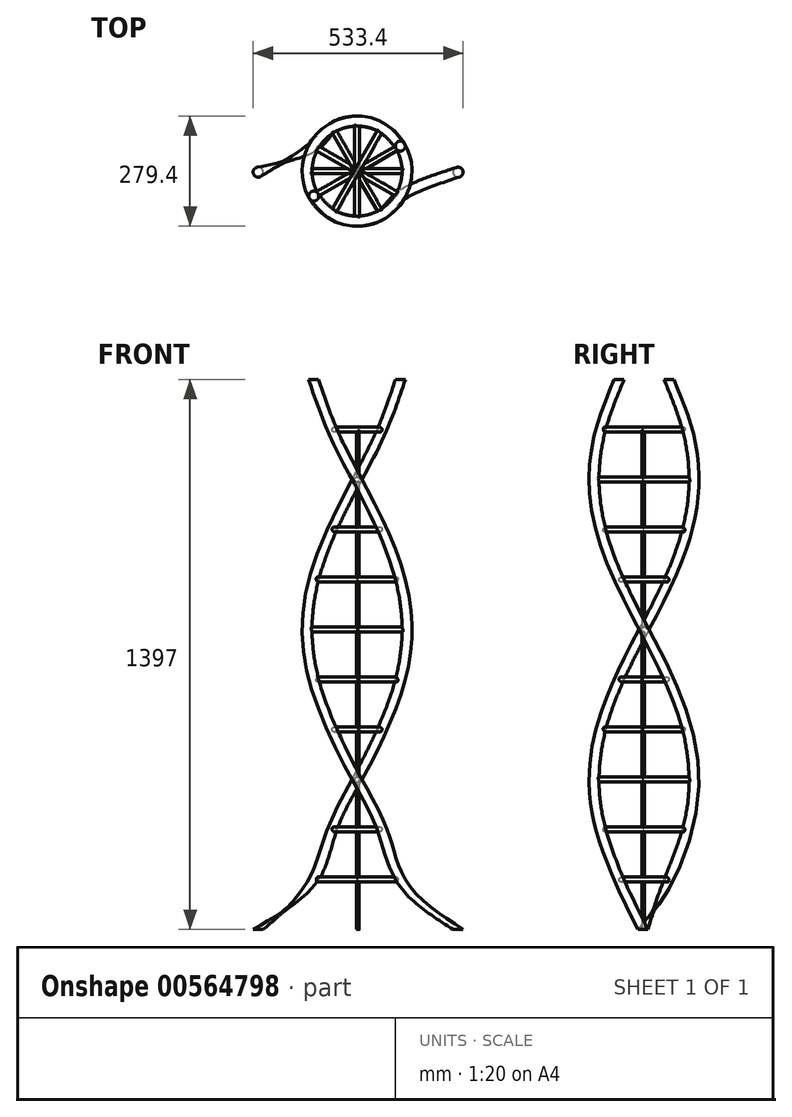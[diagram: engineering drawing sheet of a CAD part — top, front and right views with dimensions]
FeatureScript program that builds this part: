
annotation { "Feature Type Name" : "Feature", "Feature Type Description" : "" }
export const myFeature = defineFeature(function(context is Context, id is Id, definition is map)
    precondition{}
    {
        {
            var Q0;
            Q0=qCreatedBy(makeId("Top.planeOp"),FACE);
            var sketch = newSketch(context, id + "F0", { "sketchPlane" : qUnion([Q0])});
            skCircle(sketch, "E0", {"center": v(0, 0) * mm, "radius": 254 * mm, "construction": true});
            skLineSegment(sketch, "E1", {"start": v(219.97, -127) * mm, "end": v(-219.97, 127) * mm});
            skLineSegment(sketch, "E2", {"start": v(0, 0) * mm, "end": v(0, -254) * mm, "construction": true});
            skLineSegment(sketch, "E3", {"start": v(0, 0) * mm, "end": v(254, 0) * mm, "construction": true});
            skCircle(sketch, "E4", {"center": v(219.97, -127) * mm, "radius": 12.7 * mm});
            skLineSegment(sketch, "E5", {"start": v(127, -219.97) * mm, "end": v(-127, 219.97) * mm});
            skLineSegment(sketch, "E6", {"start": v(0, 254) * mm, "end": v(0, -254) * mm});
            skLineSegment(sketch, "E7.MirrorCS", {"start": v(-127, -219.97) * mm, "end": v(127, 219.97) * mm});
            skLineSegment(sketch, "E8.MirrorCS", {"start": v(-219.97, -127) * mm, "end": v(219.97, 127) * mm});
            skLineSegment(sketch, "E9", {"start": v(254, 0) * mm, "end": v(-254, 0) * mm});
            skCircle(sketch, "E10", {"center": v(127, -219.97) * mm, "radius": 12.7 * mm});
            skCircle(sketch, "E11", {"center": v(0, -254) * mm, "radius": 12.7 * mm});
            skCircle(sketch, "E12", {"center": v(-127, -219.97) * mm, "radius": 12.7 * mm});
            skCircle(sketch, "E13", {"center": v(-219.97, -127) * mm, "radius": 12.7 * mm});
            skCircle(sketch, "E14", {"center": v(-254, 0) * mm, "radius": 12.7 * mm});
            skCircle(sketch, "E15", {"center": v(-219.97, 127) * mm, "radius": 12.7 * mm});
            skCircle(sketch, "E16", {"center": v(-127, 219.97) * mm, "radius": 76.2 * mm});
            skCircle(sketch, "E17", {"center": v(0, 254) * mm, "radius": 76.2 * mm});
            skCircle(sketch, "E18", {"center": v(127, 219.97) * mm, "radius": 38.1 * mm});
            skCircle(sketch, "E19", {"center": v(219.97, 127) * mm, "radius": 38.1 * mm});
            skCircle(sketch, "E20", {"center": v(254, 0) * mm, "radius": 12.7 * mm});
            skSolve(sketch);
        }
        {
            var Q0;
            Q0=qCreatedBy(makeId("Top.planeOp"),FACE);
            cPlane(context, id + "F1", {"entities" : qUnion([Q0]), "cplaneType" : CPlaneType.OFFSET, "offset" : 127 * mm, "width" : 152.4 * mm, "height" : 152.4 * mm});
        }
        {
            var Q0;
            Q0=qCreatedBy(id+"F1.planeOp",FACE);
            cPlane(context, id + "F2", {"entities" : qUnion([Q0]), "cplaneType" : CPlaneType.OFFSET, "offset" : 127 * mm, "width" : 152.4 * mm, "height" : 152.4 * mm});
        }
        {
            var Q0;
            Q0=qCreatedBy(id+"F2.planeOp",FACE);
            cPlane(context, id + "F3", {"entities" : qUnion([Q0]), "cplaneType" : CPlaneType.OFFSET, "offset" : 127 * mm, "width" : 152.4 * mm, "height" : 152.4 * mm});
        }
        {
            var Q0;
            Q0=qCreatedBy(id+"F1.planeOp",FACE);
            var sketch = newSketch(context, id + "F4", { "sketchPlane" : qUnion([Q0])});
            skCircle(sketch, "E21", {"center": v(-2.76, 2.76) * mm, "radius": 127 * mm, "construction": true});
            skLineSegment(sketch, "E22", {"start": v(107.22, -60.74) * mm, "end": v(-112.75, 66.26) * mm});
            skLineSegment(sketch, "E23", {"start": v(-2.76, 2.76) * mm, "end": v(-2.76, -124.24) * mm, "construction": true});
            skLineSegment(sketch, "E24", {"start": v(-2.76, 2.76) * mm, "end": v(124.24, 2.76) * mm, "construction": true});
            skCircle(sketch, "E25", {"center": v(107.22, -60.74) * mm, "radius": 12.7 * mm});
            skLineSegment(sketch, "E26", {"start": v(60.74, -107.22) * mm, "end": v(-66.26, 112.75) * mm});
            skLineSegment(sketch, "E27", {"start": v(-2.76, 129.76) * mm, "end": v(-2.76, -124.24) * mm});
            skLineSegment(sketch, "E28.MirrorCS", {"start": v(-66.26, -107.22) * mm, "end": v(60.74, 112.75) * mm});
            skLineSegment(sketch, "E29.MirrorCS", {"start": v(-112.75, -60.74) * mm, "end": v(107.22, 66.26) * mm});
            skLineSegment(sketch, "E30", {"start": v(124.24, 2.76) * mm, "end": v(-129.76, 2.76) * mm});
            skCircle(sketch, "E31", {"center": v(60.74, -107.22) * mm, "radius": 12.7 * mm});
            skCircle(sketch, "E32", {"center": v(-2.76, -124.24) * mm, "radius": 12.7 * mm});
            skCircle(sketch, "E33", {"center": v(-66.26, -107.22) * mm, "radius": 12.7 * mm});
            skCircle(sketch, "E34", {"center": v(-112.75, -60.74) * mm, "radius": 12.7 * mm});
            skCircle(sketch, "E35", {"center": v(-129.76, 2.76) * mm, "radius": 12.7 * mm});
            skCircle(sketch, "E36", {"center": v(-112.75, 66.26) * mm, "radius": 12.7 * mm});
            skCircle(sketch, "E37", {"center": v(-66.26, 112.75) * mm, "radius": 12.7 * mm});
            skCircle(sketch, "E38", {"center": v(-2.76, 129.76) * mm, "radius": 12.7 * mm});
            skCircle(sketch, "E39", {"center": v(60.74, 112.75) * mm, "radius": 12.7 * mm});
            skCircle(sketch, "E40", {"center": v(107.22, 66.26) * mm, "radius": 12.7 * mm});
            skCircle(sketch, "E41", {"center": v(124.24, 2.76) * mm, "radius": 12.7 * mm});
            skSolve(sketch);
        }
        {
            var Q0;
            Q0=qCreatedBy(id+"F2.planeOp",FACE);
            var sketch = newSketch(context, id + "F5", { "sketchPlane" : qUnion([Q0])});
            skCircle(sketch, "E42", {"center": v(-2.76, 2.76) * mm, "radius": 127 * mm, "construction": true});
            skLineSegment(sketch, "E43", {"start": v(107.22, -60.74) * mm, "end": v(-112.75, 66.26) * mm});
            skLineSegment(sketch, "E44", {"start": v(-2.76, 2.76) * mm, "end": v(-2.76, -124.24) * mm, "construction": true});
            skLineSegment(sketch, "E45", {"start": v(-2.76, 2.76) * mm, "end": v(124.24, 2.76) * mm, "construction": true});
            skCircle(sketch, "E46", {"center": v(107.22, -60.74) * mm, "radius": 12.7 * mm});
            skLineSegment(sketch, "E47", {"start": v(60.74, -107.22) * mm, "end": v(-66.26, 112.75) * mm});
            skLineSegment(sketch, "E48", {"start": v(-2.76, 129.76) * mm, "end": v(-2.76, -124.24) * mm});
            skLineSegment(sketch, "E49.MirrorCS", {"start": v(-66.26, -107.22) * mm, "end": v(60.74, 112.75) * mm});
            skLineSegment(sketch, "E50.MirrorCS", {"start": v(-112.75, -60.74) * mm, "end": v(107.22, 66.26) * mm});
            skLineSegment(sketch, "E51", {"start": v(124.24, 2.76) * mm, "end": v(-129.76, 2.76) * mm});
            skCircle(sketch, "E52", {"center": v(60.74, -107.22) * mm, "radius": 12.7 * mm});
            skCircle(sketch, "E53", {"center": v(-2.76, -124.24) * mm, "radius": 12.7 * mm});
            skCircle(sketch, "E54", {"center": v(-66.26, -107.22) * mm, "radius": 12.7 * mm});
            skCircle(sketch, "E55", {"center": v(-112.75, -60.74) * mm, "radius": 12.7 * mm});
            skCircle(sketch, "E56", {"center": v(-129.76, 2.76) * mm, "radius": 12.7 * mm});
            skCircle(sketch, "E57", {"center": v(-112.75, 66.26) * mm, "radius": 12.7 * mm});
            skCircle(sketch, "E58", {"center": v(-66.26, 112.75) * mm, "radius": 12.7 * mm});
            skCircle(sketch, "E59", {"center": v(-2.76, 129.76) * mm, "radius": 12.7 * mm});
            skCircle(sketch, "E60", {"center": v(60.74, 112.75) * mm, "radius": 12.7 * mm});
            skCircle(sketch, "E61", {"center": v(107.22, 66.26) * mm, "radius": 12.7 * mm});
            skCircle(sketch, "E62", {"center": v(124.24, 2.76) * mm, "radius": 12.7 * mm});
            skSolve(sketch);
        }
        {
            var Q0;
            Q0=qCreatedBy(id+"F3.planeOp",FACE);
            var sketch = newSketch(context, id + "F6", { "sketchPlane" : qUnion([Q0])});
            skCircle(sketch, "E63", {"center": v(-2.76, 2.76) * mm, "radius": 127 * mm, "construction": true});
            skLineSegment(sketch, "E64", {"start": v(107.22, -60.74) * mm, "end": v(-112.75, 66.26) * mm});
            skLineSegment(sketch, "E65", {"start": v(-2.76, 2.76) * mm, "end": v(-2.76, -124.24) * mm, "construction": true});
            skLineSegment(sketch, "E66", {"start": v(-2.76, 2.76) * mm, "end": v(124.24, 2.76) * mm, "construction": true});
            skCircle(sketch, "E67", {"center": v(107.22, -60.74) * mm, "radius": 12.7 * mm});
            skLineSegment(sketch, "E68", {"start": v(60.74, -107.22) * mm, "end": v(-66.26, 112.75) * mm});
            skLineSegment(sketch, "E69", {"start": v(-2.76, 129.76) * mm, "end": v(-2.76, -124.24) * mm});
            skLineSegment(sketch, "E70.MirrorCS", {"start": v(-66.26, -107.22) * mm, "end": v(60.74, 112.75) * mm});
            skLineSegment(sketch, "E71.MirrorCS", {"start": v(-112.75, -60.74) * mm, "end": v(107.22, 66.26) * mm});
            skLineSegment(sketch, "E72", {"start": v(124.24, 2.76) * mm, "end": v(-129.76, 2.76) * mm});
            skCircle(sketch, "E73", {"center": v(60.74, -107.22) * mm, "radius": 12.7 * mm});
            skCircle(sketch, "E74", {"center": v(-2.76, -124.24) * mm, "radius": 12.7 * mm});
            skCircle(sketch, "E75", {"center": v(-66.26, -107.22) * mm, "radius": 12.7 * mm});
            skCircle(sketch, "E76", {"center": v(-112.75, -60.74) * mm, "radius": 12.7 * mm});
            skCircle(sketch, "E77", {"center": v(-129.76, 2.76) * mm, "radius": 12.7 * mm});
            skCircle(sketch, "E78", {"center": v(-112.75, 66.26) * mm, "radius": 12.7 * mm});
            skCircle(sketch, "E79", {"center": v(-66.26, 112.75) * mm, "radius": 12.7 * mm});
            skCircle(sketch, "E80", {"center": v(-2.76, 129.76) * mm, "radius": 12.7 * mm});
            skCircle(sketch, "E81", {"center": v(60.74, 112.75) * mm, "radius": 12.7 * mm});
            skCircle(sketch, "E82", {"center": v(107.22, 66.26) * mm, "radius": 12.7 * mm});
            skCircle(sketch, "E83", {"center": v(124.24, 2.76) * mm, "radius": 12.7 * mm});
            skSolve(sketch);
        }
        {
            var Q0;
            Q0=qCreatedBy(id+"F3.planeOp",FACE);
            cPlane(context, id + "F7", {"entities" : qUnion([Q0]), "cplaneType" : CPlaneType.OFFSET, "offset" : 127 * mm, "width" : 152.4 * mm, "height" : 152.4 * mm});
        }
        {
            var Q0;
            Q0=qCreatedBy(id+"F7.planeOp",FACE);
            cPlane(context, id + "F8", {"entities" : qUnion([Q0]), "cplaneType" : CPlaneType.OFFSET, "offset" : 127 * mm, "width" : 152.4 * mm, "height" : 152.4 * mm});
        }
        {
            var Q0;
            Q0=qCreatedBy(id+"F8.planeOp",FACE);
            cPlane(context, id + "F9", {"entities" : qUnion([Q0]), "cplaneType" : CPlaneType.OFFSET, "offset" : 127 * mm, "width" : 152.4 * mm, "height" : 152.4 * mm});
        }
        {
            var Q0;
            Q0=qCreatedBy(id+"F9.planeOp",FACE);
            cPlane(context, id + "F10", {"entities" : qUnion([Q0]), "cplaneType" : CPlaneType.OFFSET, "offset" : 127 * mm, "width" : 152.4 * mm, "height" : 152.4 * mm});
        }
        {
            var Q0;
            Q0=qCreatedBy(id+"F10.planeOp",FACE);
            cPlane(context, id + "F11", {"entities" : qUnion([Q0]), "cplaneType" : CPlaneType.OFFSET, "offset" : 127 * mm, "width" : 152.4 * mm, "height" : 152.4 * mm});
        }
        {
            var Q0;
            Q0=qCreatedBy(id+"F11.planeOp",FACE);
            cPlane(context, id + "F12", {"entities" : qUnion([Q0]), "cplaneType" : CPlaneType.OFFSET, "offset" : 127 * mm, "width" : 152.4 * mm, "height" : 152.4 * mm});
        }
        {
            var Q0;
            Q0=qCreatedBy(id+"F12.planeOp",FACE);
            cPlane(context, id + "F13", {"entities" : qUnion([Q0]), "cplaneType" : CPlaneType.OFFSET, "offset" : 127 * mm, "width" : 152.4 * mm, "height" : 152.4 * mm});
        }
        {
            var Q0;
            Q0=qCreatedBy(id+"F13.planeOp",FACE);
            cPlane(context, id + "F14", {"entities" : qUnion([Q0]), "cplaneType" : CPlaneType.OFFSET, "offset" : 127 * mm, "width" : 152.4 * mm, "height" : 152.4 * mm});
        }
        {
            var Q0;
            Q0=qCreatedBy(id+"F7.planeOp",FACE);
            var sketch = newSketch(context, id + "F15", { "sketchPlane" : qUnion([Q0])});
            skCircle(sketch, "E84", {"center": v(-2.76, 2.76) * mm, "radius": 127 * mm, "construction": true});
            skLineSegment(sketch, "E85", {"start": v(107.22, -60.74) * mm, "end": v(-112.75, 66.26) * mm});
            skLineSegment(sketch, "E86", {"start": v(-2.76, 2.76) * mm, "end": v(-2.76, -124.24) * mm, "construction": true});
            skLineSegment(sketch, "E87", {"start": v(-2.76, 2.76) * mm, "end": v(124.24, 2.76) * mm, "construction": true});
            skCircle(sketch, "E88", {"center": v(107.22, -60.74) * mm, "radius": 12.7 * mm});
            skLineSegment(sketch, "E89", {"start": v(60.74, -107.22) * mm, "end": v(-66.26, 112.75) * mm});
            skLineSegment(sketch, "E90", {"start": v(-2.76, 129.76) * mm, "end": v(-2.76, -124.24) * mm});
            skLineSegment(sketch, "E91.MirrorCS", {"start": v(-66.26, -107.22) * mm, "end": v(60.74, 112.75) * mm});
            skLineSegment(sketch, "E92.MirrorCS", {"start": v(-112.75, -60.74) * mm, "end": v(107.22, 66.26) * mm});
            skLineSegment(sketch, "E93", {"start": v(124.24, 2.76) * mm, "end": v(-129.76, 2.76) * mm});
            skCircle(sketch, "E94", {"center": v(60.74, -107.22) * mm, "radius": 12.7 * mm});
            skCircle(sketch, "E95", {"center": v(-2.76, -124.24) * mm, "radius": 12.7 * mm});
            skCircle(sketch, "E96", {"center": v(-66.26, -107.22) * mm, "radius": 12.7 * mm});
            skCircle(sketch, "E97", {"center": v(-112.75, -60.74) * mm, "radius": 12.7 * mm});
            skCircle(sketch, "E98", {"center": v(-129.76, 2.76) * mm, "radius": 12.7 * mm});
            skCircle(sketch, "E99", {"center": v(-112.75, 66.26) * mm, "radius": 12.7 * mm});
            skCircle(sketch, "E100", {"center": v(-66.26, 112.75) * mm, "radius": 12.7 * mm});
            skCircle(sketch, "E101", {"center": v(-2.76, 129.76) * mm, "radius": 12.7 * mm});
            skCircle(sketch, "E102", {"center": v(60.74, 112.75) * mm, "radius": 12.7 * mm});
            skCircle(sketch, "E103", {"center": v(107.22, 66.26) * mm, "radius": 12.7 * mm});
            skCircle(sketch, "E104", {"center": v(124.24, 2.76) * mm, "radius": 12.7 * mm});
            skSolve(sketch);
        }
        {
            var Q0;
            Q0=qCreatedBy(id+"F8.planeOp",FACE);
            var sketch = newSketch(context, id + "F16", { "sketchPlane" : qUnion([Q0])});
            skCircle(sketch, "E105", {"center": v(-2.76, 2.76) * mm, "radius": 127 * mm, "construction": true});
            skLineSegment(sketch, "E106", {"start": v(107.22, -60.74) * mm, "end": v(-112.75, 66.26) * mm});
            skLineSegment(sketch, "E107", {"start": v(-2.76, 2.76) * mm, "end": v(-2.76, -124.24) * mm, "construction": true});
            skLineSegment(sketch, "E108", {"start": v(-2.76, 2.76) * mm, "end": v(124.24, 2.76) * mm, "construction": true});
            skCircle(sketch, "E109", {"center": v(107.22, -60.74) * mm, "radius": 12.7 * mm});
            skLineSegment(sketch, "E110", {"start": v(60.74, -107.22) * mm, "end": v(-66.26, 112.75) * mm});
            skLineSegment(sketch, "E111", {"start": v(-2.76, 129.76) * mm, "end": v(-2.76, -124.24) * mm});
            skLineSegment(sketch, "E112.MirrorCS", {"start": v(-66.26, -107.22) * mm, "end": v(60.74, 112.75) * mm});
            skLineSegment(sketch, "E113.MirrorCS", {"start": v(-112.75, -60.74) * mm, "end": v(107.22, 66.26) * mm});
            skLineSegment(sketch, "E114", {"start": v(124.24, 2.76) * mm, "end": v(-129.76, 2.76) * mm});
            skCircle(sketch, "E115", {"center": v(60.74, -107.22) * mm, "radius": 12.7 * mm});
            skCircle(sketch, "E116", {"center": v(-2.76, -124.24) * mm, "radius": 12.7 * mm});
            skCircle(sketch, "E117", {"center": v(-66.26, -107.22) * mm, "radius": 12.7 * mm});
            skCircle(sketch, "E118", {"center": v(-112.75, -60.74) * mm, "radius": 12.7 * mm});
            skCircle(sketch, "E119", {"center": v(-129.76, 2.76) * mm, "radius": 12.7 * mm});
            skCircle(sketch, "E120", {"center": v(-112.75, 66.26) * mm, "radius": 12.7 * mm});
            skCircle(sketch, "E121", {"center": v(-66.26, 112.75) * mm, "radius": 12.7 * mm});
            skCircle(sketch, "E122", {"center": v(-2.76, 129.76) * mm, "radius": 12.7 * mm});
            skCircle(sketch, "E123", {"center": v(60.74, 112.75) * mm, "radius": 12.7 * mm});
            skCircle(sketch, "E124", {"center": v(107.22, 66.26) * mm, "radius": 12.7 * mm});
            skCircle(sketch, "E125", {"center": v(124.24, 2.76) * mm, "radius": 12.7 * mm});
            skSolve(sketch);
        }
        {
            var Q0;
            Q0=qCreatedBy(id+"F9.planeOp",FACE);
            var sketch = newSketch(context, id + "F17", { "sketchPlane" : qUnion([Q0])});
            skCircle(sketch, "E126", {"center": v(-2.76, 2.76) * mm, "radius": 127 * mm, "construction": true});
            skLineSegment(sketch, "E127", {"start": v(107.22, -60.74) * mm, "end": v(-112.75, 66.26) * mm});
            skLineSegment(sketch, "E128", {"start": v(-2.76, 2.76) * mm, "end": v(-2.76, -124.24) * mm, "construction": true});
            skLineSegment(sketch, "E129", {"start": v(-2.76, 2.76) * mm, "end": v(124.24, 2.76) * mm, "construction": true});
            skCircle(sketch, "E130", {"center": v(107.22, -60.74) * mm, "radius": 12.7 * mm});
            skLineSegment(sketch, "E131", {"start": v(60.74, -107.22) * mm, "end": v(-66.26, 112.75) * mm});
            skLineSegment(sketch, "E132", {"start": v(-2.76, 129.76) * mm, "end": v(-2.76, -124.24) * mm});
            skLineSegment(sketch, "E133.MirrorCS", {"start": v(-66.26, -107.22) * mm, "end": v(60.74, 112.75) * mm});
            skLineSegment(sketch, "E134.MirrorCS", {"start": v(-112.75, -60.74) * mm, "end": v(107.22, 66.26) * mm});
            skLineSegment(sketch, "E135", {"start": v(124.24, 2.76) * mm, "end": v(-129.76, 2.76) * mm});
            skCircle(sketch, "E136", {"center": v(60.74, -107.22) * mm, "radius": 12.7 * mm});
            skCircle(sketch, "E137", {"center": v(-2.76, -124.24) * mm, "radius": 12.7 * mm});
            skCircle(sketch, "E138", {"center": v(-66.26, -107.22) * mm, "radius": 12.7 * mm});
            skCircle(sketch, "E139", {"center": v(-112.75, -60.74) * mm, "radius": 12.7 * mm});
            skCircle(sketch, "E140", {"center": v(-129.76, 2.76) * mm, "radius": 12.7 * mm});
            skCircle(sketch, "E141", {"center": v(-112.75, 66.26) * mm, "radius": 12.7 * mm});
            skCircle(sketch, "E142", {"center": v(-66.26, 112.75) * mm, "radius": 12.7 * mm});
            skCircle(sketch, "E143", {"center": v(-2.76, 129.76) * mm, "radius": 12.7 * mm});
            skCircle(sketch, "E144", {"center": v(60.74, 112.75) * mm, "radius": 12.7 * mm});
            skCircle(sketch, "E145", {"center": v(107.22, 66.26) * mm, "radius": 12.7 * mm});
            skCircle(sketch, "E146", {"center": v(124.24, 2.76) * mm, "radius": 12.7 * mm});
            skSolve(sketch);
        }
        {
            var Q0;
            Q0=qCreatedBy(id+"F10.planeOp",FACE);
            var sketch = newSketch(context, id + "F18", { "sketchPlane" : qUnion([Q0])});
            skCircle(sketch, "E147", {"center": v(-2.76, 2.76) * mm, "radius": 127 * mm, "construction": true});
            skLineSegment(sketch, "E148", {"start": v(107.22, -60.74) * mm, "end": v(-112.75, 66.26) * mm});
            skLineSegment(sketch, "E149", {"start": v(-2.76, 2.76) * mm, "end": v(-2.76, -124.24) * mm, "construction": true});
            skLineSegment(sketch, "E150", {"start": v(-2.76, 2.76) * mm, "end": v(124.24, 2.76) * mm, "construction": true});
            skCircle(sketch, "E151", {"center": v(107.22, -60.74) * mm, "radius": 12.7 * mm});
            skLineSegment(sketch, "E152", {"start": v(60.74, -107.22) * mm, "end": v(-66.26, 112.75) * mm});
            skLineSegment(sketch, "E153", {"start": v(-2.76, 129.76) * mm, "end": v(-2.76, -124.24) * mm});
            skLineSegment(sketch, "E154.MirrorCS", {"start": v(-66.26, -107.22) * mm, "end": v(60.74, 112.75) * mm});
            skLineSegment(sketch, "E155.MirrorCS", {"start": v(-112.75, -60.74) * mm, "end": v(107.22, 66.26) * mm});
            skLineSegment(sketch, "E156", {"start": v(124.24, 2.76) * mm, "end": v(-129.76, 2.76) * mm});
            skCircle(sketch, "E157", {"center": v(60.74, -107.22) * mm, "radius": 12.7 * mm});
            skCircle(sketch, "E158", {"center": v(-2.76, -124.24) * mm, "radius": 12.7 * mm});
            skCircle(sketch, "E159", {"center": v(-66.26, -107.22) * mm, "radius": 12.7 * mm});
            skCircle(sketch, "E160", {"center": v(-112.75, -60.74) * mm, "radius": 12.7 * mm});
            skCircle(sketch, "E161", {"center": v(-129.76, 2.76) * mm, "radius": 12.7 * mm});
            skCircle(sketch, "E162", {"center": v(-112.75, 66.26) * mm, "radius": 12.7 * mm});
            skCircle(sketch, "E163", {"center": v(-66.26, 112.75) * mm, "radius": 12.7 * mm});
            skCircle(sketch, "E164", {"center": v(-2.76, 129.76) * mm, "radius": 12.7 * mm});
            skCircle(sketch, "E165", {"center": v(60.74, 112.75) * mm, "radius": 12.7 * mm});
            skCircle(sketch, "E166", {"center": v(107.22, 66.26) * mm, "radius": 12.7 * mm});
            skCircle(sketch, "E167", {"center": v(124.24, 2.76) * mm, "radius": 12.7 * mm});
            skSolve(sketch);
        }
        {
            var Q0;
            Q0=qCreatedBy(id+"F11.planeOp",FACE);
            var sketch = newSketch(context, id + "F19", { "sketchPlane" : qUnion([Q0])});
            skCircle(sketch, "E168", {"center": v(-2.76, 2.76) * mm, "radius": 127 * mm, "construction": true});
            skLineSegment(sketch, "E169", {"start": v(107.22, -60.74) * mm, "end": v(-112.75, 66.26) * mm});
            skLineSegment(sketch, "E170", {"start": v(-2.76, 2.76) * mm, "end": v(-2.76, -124.24) * mm, "construction": true});
            skLineSegment(sketch, "E171", {"start": v(-2.76, 2.76) * mm, "end": v(124.24, 2.76) * mm, "construction": true});
            skCircle(sketch, "E172", {"center": v(107.22, -60.74) * mm, "radius": 12.7 * mm});
            skLineSegment(sketch, "E173", {"start": v(60.74, -107.22) * mm, "end": v(-66.26, 112.75) * mm});
            skLineSegment(sketch, "E174", {"start": v(-2.76, 129.76) * mm, "end": v(-2.76, -124.24) * mm});
            skLineSegment(sketch, "E175.MirrorCS", {"start": v(-66.26, -107.22) * mm, "end": v(60.74, 112.75) * mm});
            skLineSegment(sketch, "E176.MirrorCS", {"start": v(-112.75, -60.74) * mm, "end": v(107.22, 66.26) * mm});
            skLineSegment(sketch, "E177", {"start": v(124.24, 2.76) * mm, "end": v(-129.76, 2.76) * mm});
            skCircle(sketch, "E178", {"center": v(60.74, -107.22) * mm, "radius": 12.7 * mm});
            skCircle(sketch, "E179", {"center": v(-2.76, -124.24) * mm, "radius": 12.7 * mm});
            skCircle(sketch, "E180", {"center": v(-66.26, -107.22) * mm, "radius": 12.7 * mm});
            skCircle(sketch, "E181", {"center": v(-112.75, -60.74) * mm, "radius": 12.7 * mm});
            skCircle(sketch, "E182", {"center": v(-129.76, 2.76) * mm, "radius": 12.7 * mm});
            skCircle(sketch, "E183", {"center": v(-112.75, 66.26) * mm, "radius": 12.7 * mm});
            skCircle(sketch, "E184", {"center": v(-66.26, 112.75) * mm, "radius": 12.7 * mm});
            skCircle(sketch, "E185", {"center": v(-2.76, 129.76) * mm, "radius": 12.7 * mm});
            skCircle(sketch, "E186", {"center": v(60.74, 112.75) * mm, "radius": 12.7 * mm});
            skCircle(sketch, "E187", {"center": v(107.22, 66.26) * mm, "radius": 12.7 * mm});
            skCircle(sketch, "E188", {"center": v(124.24, 2.76) * mm, "radius": 12.7 * mm});
            skSolve(sketch);
        }
        {
            var Q0;
            Q0=qCreatedBy(id+"F12.planeOp",FACE);
            var sketch = newSketch(context, id + "F20", { "sketchPlane" : qUnion([Q0])});
            skCircle(sketch, "E189", {"center": v(-2.76, 2.76) * mm, "radius": 127 * mm, "construction": true});
            skLineSegment(sketch, "E190", {"start": v(107.22, -60.74) * mm, "end": v(-112.75, 66.26) * mm});
            skLineSegment(sketch, "E191", {"start": v(-2.76, 2.76) * mm, "end": v(-2.76, -124.24) * mm, "construction": true});
            skLineSegment(sketch, "E192", {"start": v(-2.76, 2.76) * mm, "end": v(124.24, 2.76) * mm, "construction": true});
            skCircle(sketch, "E193", {"center": v(107.22, -60.74) * mm, "radius": 12.7 * mm});
            skLineSegment(sketch, "E194", {"start": v(60.74, -107.22) * mm, "end": v(-66.26, 112.75) * mm});
            skLineSegment(sketch, "E195", {"start": v(-2.76, 129.76) * mm, "end": v(-2.76, -124.24) * mm});
            skLineSegment(sketch, "E196.MirrorCS", {"start": v(-66.26, -107.22) * mm, "end": v(60.74, 112.75) * mm});
            skLineSegment(sketch, "E197.MirrorCS", {"start": v(-112.75, -60.74) * mm, "end": v(107.22, 66.26) * mm});
            skLineSegment(sketch, "E198", {"start": v(124.24, 2.76) * mm, "end": v(-129.76, 2.76) * mm});
            skCircle(sketch, "E199", {"center": v(60.74, -107.22) * mm, "radius": 12.7 * mm});
            skCircle(sketch, "E200", {"center": v(-2.76, -124.24) * mm, "radius": 12.7 * mm});
            skCircle(sketch, "E201", {"center": v(-66.26, -107.22) * mm, "radius": 12.7 * mm});
            skCircle(sketch, "E202", {"center": v(-112.75, -60.74) * mm, "radius": 12.7 * mm});
            skCircle(sketch, "E203", {"center": v(-129.76, 2.76) * mm, "radius": 12.7 * mm});
            skCircle(sketch, "E204", {"center": v(-112.75, 66.26) * mm, "radius": 12.7 * mm});
            skCircle(sketch, "E205", {"center": v(-66.26, 112.75) * mm, "radius": 12.7 * mm});
            skCircle(sketch, "E206", {"center": v(-2.76, 129.76) * mm, "radius": 12.7 * mm});
            skCircle(sketch, "E207", {"center": v(60.74, 112.75) * mm, "radius": 12.7 * mm});
            skCircle(sketch, "E208", {"center": v(107.22, 66.26) * mm, "radius": 12.7 * mm});
            skCircle(sketch, "E209", {"center": v(124.24, 2.76) * mm, "radius": 12.7 * mm});
            skSolve(sketch);
        }
        {
            var Q0;
            Q0=qCreatedBy(id+"F13.planeOp",FACE);
            var sketch = newSketch(context, id + "F21", { "sketchPlane" : qUnion([Q0])});
            skCircle(sketch, "E210", {"center": v(-2.76, 2.76) * mm, "radius": 127 * mm, "construction": true});
            skLineSegment(sketch, "E211", {"start": v(107.22, -60.74) * mm, "end": v(-112.75, 66.26) * mm});
            skLineSegment(sketch, "E212", {"start": v(-2.76, 2.76) * mm, "end": v(-2.76, -124.24) * mm, "construction": true});
            skLineSegment(sketch, "E213", {"start": v(-2.76, 2.76) * mm, "end": v(124.24, 2.76) * mm, "construction": true});
            skCircle(sketch, "E214", {"center": v(107.22, -60.74) * mm, "radius": 12.7 * mm});
            skLineSegment(sketch, "E215", {"start": v(60.74, -107.22) * mm, "end": v(-66.26, 112.75) * mm});
            skLineSegment(sketch, "E216", {"start": v(-2.76, 129.76) * mm, "end": v(-2.76, -124.24) * mm});
            skLineSegment(sketch, "E217.MirrorCS", {"start": v(-66.26, -107.22) * mm, "end": v(60.74, 112.75) * mm});
            skLineSegment(sketch, "E218.MirrorCS", {"start": v(-112.75, -60.74) * mm, "end": v(107.22, 66.26) * mm});
            skLineSegment(sketch, "E219", {"start": v(124.24, 2.76) * mm, "end": v(-129.76, 2.76) * mm});
            skCircle(sketch, "E220", {"center": v(60.74, -107.22) * mm, "radius": 12.7 * mm});
            skCircle(sketch, "E221", {"center": v(-2.76, -124.24) * mm, "radius": 12.7 * mm});
            skCircle(sketch, "E222", {"center": v(-66.26, -107.22) * mm, "radius": 12.7 * mm});
            skCircle(sketch, "E223", {"center": v(-112.75, -60.74) * mm, "radius": 12.7 * mm});
            skCircle(sketch, "E224", {"center": v(-129.76, 2.76) * mm, "radius": 12.7 * mm});
            skCircle(sketch, "E225", {"center": v(-112.75, 66.26) * mm, "radius": 12.7 * mm});
            skCircle(sketch, "E226", {"center": v(-66.26, 112.75) * mm, "radius": 12.7 * mm});
            skCircle(sketch, "E227", {"center": v(-2.76, 129.76) * mm, "radius": 12.7 * mm});
            skCircle(sketch, "E228", {"center": v(60.74, 112.75) * mm, "radius": 12.7 * mm});
            skCircle(sketch, "E229", {"center": v(107.22, 66.26) * mm, "radius": 12.7 * mm});
            skCircle(sketch, "E230", {"center": v(124.24, 2.76) * mm, "radius": 12.7 * mm});
            skSolve(sketch);
        }
        {
            var Q0;
            Q0=qCreatedBy(id+"F14.planeOp",FACE);
            var sketch = newSketch(context, id + "F22", { "sketchPlane" : qUnion([Q0])});
            skCircle(sketch, "E231", {"center": v(-2.76, 2.76) * mm, "radius": 127 * mm, "construction": true});
            skLineSegment(sketch, "E232", {"start": v(107.22, -60.74) * mm, "end": v(-112.75, 66.26) * mm});
            skLineSegment(sketch, "E233", {"start": v(-2.76, 2.76) * mm, "end": v(-2.76, -124.24) * mm, "construction": true});
            skLineSegment(sketch, "E234", {"start": v(-2.76, 2.76) * mm, "end": v(124.24, 2.76) * mm, "construction": true});
            skCircle(sketch, "E235", {"center": v(107.22, -60.74) * mm, "radius": 12.7 * mm});
            skLineSegment(sketch, "E236", {"start": v(60.74, -107.22) * mm, "end": v(-66.26, 112.75) * mm});
            skLineSegment(sketch, "E237", {"start": v(-2.76, 129.76) * mm, "end": v(-2.76, -124.24) * mm});
            skLineSegment(sketch, "E238.MirrorCS", {"start": v(-66.26, -107.22) * mm, "end": v(60.74, 112.75) * mm});
            skLineSegment(sketch, "E239.MirrorCS", {"start": v(-112.75, -60.74) * mm, "end": v(107.22, 66.26) * mm});
            skLineSegment(sketch, "E240", {"start": v(124.24, 2.76) * mm, "end": v(-129.76, 2.76) * mm});
            skCircle(sketch, "E241", {"center": v(60.74, -107.22) * mm, "radius": 12.7 * mm});
            skCircle(sketch, "E242", {"center": v(-2.76, -124.24) * mm, "radius": 12.7 * mm});
            skCircle(sketch, "E243", {"center": v(-66.26, -107.22) * mm, "radius": 12.7 * mm});
            skCircle(sketch, "E244", {"center": v(-112.75, -60.74) * mm, "radius": 12.7 * mm});
            skCircle(sketch, "E245", {"center": v(-129.76, 2.76) * mm, "radius": 12.7 * mm});
            skCircle(sketch, "E246", {"center": v(-112.75, 66.26) * mm, "radius": 12.7 * mm});
            skCircle(sketch, "E247", {"center": v(-66.26, 112.75) * mm, "radius": 12.7 * mm});
            skCircle(sketch, "E248", {"center": v(-2.76, 129.76) * mm, "radius": 12.7 * mm});
            skCircle(sketch, "E249", {"center": v(60.74, 112.75) * mm, "radius": 12.7 * mm});
            skCircle(sketch, "E250", {"center": v(107.22, 66.26) * mm, "radius": 12.7 * mm});
            skCircle(sketch, "E251", {"center": v(124.24, 2.76) * mm, "radius": 12.7 * mm});
            skSolve(sketch);
        }
        {
            var Q0;
            Q0=makeQuery(id+"F0.imprint","IMPRINT",FACE,{"disambiguationData":[TD([[makeQuery(id+"F0.imprint","IMPRINT",EDGE,{"derivedFrom":sQuery(id+"F0.wireOp",EDGE,"E14")}),1.0]])]});
            var Q1;
            Q1=makeQuery(id+"F4.imprint","IMPRINT",FACE,{"disambiguationData":[TD([[makeQuery(id+"F4.imprint","IMPRINT",EDGE,{"derivedFrom":sQuery(id+"F4.wireOp",EDGE,"E36")}),1.0]])]});
            var Q2;
            Q2=makeQuery(id+"F5.imprint","IMPRINT",FACE,{"disambiguationData":[TD([[makeQuery(id+"F5.imprint","IMPRINT",EDGE,{"derivedFrom":sQuery(id+"F5.wireOp",EDGE,"E58")}),1.0]])]});
            var Q3;
            Q3=makeQuery(id+"F6.imprint","IMPRINT",FACE,{"disambiguationData":[TD([[makeQuery(id+"F6.imprint","IMPRINT",EDGE,{"derivedFrom":sQuery(id+"F6.wireOp",EDGE,"E80")}),1.0]])]});
            var Q4;
            Q4=makeQuery(id+"F15.imprint","IMPRINT",FACE,{"disambiguationData":[TD([[makeQuery(id+"F15.imprint","IMPRINT",EDGE,{"derivedFrom":sQuery(id+"F15.wireOp",EDGE,"E102")}),1.0]])]});
            var Q5;
            Q5=makeQuery(id+"F16.imprint","IMPRINT",FACE,{"disambiguationData":[TD([[makeQuery(id+"F16.imprint","IMPRINT",EDGE,{"derivedFrom":sQuery(id+"F16.wireOp",EDGE,"E124")}),1.0]])]});
            var Q6;
            Q6=makeQuery(id+"F17.imprint","IMPRINT",FACE,{"disambiguationData":[TD([[makeQuery(id+"F17.imprint","IMPRINT",EDGE,{"derivedFrom":sQuery(id+"F17.wireOp",EDGE,"E146")}),1.0]])]});
            var Q7;
            Q7=makeQuery(id+"F18.imprint","IMPRINT",FACE,{"disambiguationData":[TD([[makeQuery(id+"F18.imprint","IMPRINT",EDGE,{"derivedFrom":sQuery(id+"F18.wireOp",EDGE,"E151")}),1.0]])]});
            var Q8;
            Q8=makeQuery(id+"F19.imprint","IMPRINT",FACE,{"disambiguationData":[TD([[makeQuery(id+"F19.imprint","IMPRINT",EDGE,{"derivedFrom":sQuery(id+"F19.wireOp",EDGE,"E178")}),1.0]])]});
            var Q9;
            Q9=makeQuery(id+"F20.imprint","IMPRINT",FACE,{"disambiguationData":[TD([[makeQuery(id+"F20.imprint","IMPRINT",EDGE,{"derivedFrom":sQuery(id+"F20.wireOp",EDGE,"E200")}),1.0]])]});
            var Q10;
            Q10=makeQuery(id+"F21.imprint","IMPRINT",FACE,{"disambiguationData":[TD([[makeQuery(id+"F21.imprint","IMPRINT",EDGE,{"derivedFrom":sQuery(id+"F21.wireOp",EDGE,"E222")}),1.0]])]});
            var Q11;
            Q11=makeQuery(id+"F22.imprint","IMPRINT",FACE,{"disambiguationData":[TD([[makeQuery(id+"F22.imprint","IMPRINT",EDGE,{"derivedFrom":sQuery(id+"F22.wireOp",EDGE,"E244")}),1.0]])]});
            loft(context, id + "F23", {"sheetProfilesArray" : [{ "sheetProfileEntities" : qUnion([Q0]) }, { "sheetProfileEntities" : qUnion([Q1]) }, { "sheetProfileEntities" : qUnion([Q2]) }, { "sheetProfileEntities" : qUnion([Q3]) }, { "sheetProfileEntities" : qUnion([Q4]) }, { "sheetProfileEntities" : qUnion([Q5]) }, { "sheetProfileEntities" : qUnion([Q6]) }, { "sheetProfileEntities" : qUnion([Q7]) }, { "sheetProfileEntities" : qUnion([Q8]) }, { "sheetProfileEntities" : qUnion([Q9]) }, { "sheetProfileEntities" : qUnion([Q10]) }, { "sheetProfileEntities" : qUnion([Q11]) }]});
        }
        {
            var Q0;
            Q0=makeQuery(id+"F0.imprint","IMPRINT",FACE,{"disambiguationData":[TD([[makeQuery(id+"F0.imprint","IMPRINT",EDGE,{"derivedFrom":sQuery(id+"F0.wireOp",EDGE,"E20")}),1.0]])]});
            var Q1;
            Q1=makeQuery(id+"F4.imprint","IMPRINT",FACE,{"disambiguationData":[TD([[makeQuery(id+"F4.imprint","IMPRINT",EDGE,{"derivedFrom":sQuery(id+"F4.wireOp",EDGE,"E25")}),1.0]])]});
            var Q2;
            Q2=makeQuery(id+"F5.imprint","IMPRINT",FACE,{"disambiguationData":[TD([[makeQuery(id+"F5.imprint","IMPRINT",EDGE,{"derivedFrom":sQuery(id+"F5.wireOp",EDGE,"E52")}),1.0]])]});
            var Q3;
            Q3=makeQuery(id+"F6.imprint","IMPRINT",FACE,{"disambiguationData":[TD([[makeQuery(id+"F6.imprint","IMPRINT",EDGE,{"derivedFrom":sQuery(id+"F6.wireOp",EDGE,"E74")}),1.0]])]});
            var Q4;
            Q4=makeQuery(id+"F15.imprint","IMPRINT",FACE,{"disambiguationData":[TD([[makeQuery(id+"F15.imprint","IMPRINT",EDGE,{"derivedFrom":sQuery(id+"F15.wireOp",EDGE,"E96")}),1.0]])]});
            var Q5;
            Q5=makeQuery(id+"F16.imprint","IMPRINT",FACE,{"disambiguationData":[TD([[makeQuery(id+"F16.imprint","IMPRINT",EDGE,{"derivedFrom":sQuery(id+"F16.wireOp",EDGE,"E118")}),1.0]])]});
            var Q6;
            Q6=makeQuery(id+"F17.imprint","IMPRINT",FACE,{"disambiguationData":[TD([[makeQuery(id+"F17.imprint","IMPRINT",EDGE,{"derivedFrom":sQuery(id+"F17.wireOp",EDGE,"E140")}),1.0]])]});
            var Q7;
            Q7=makeQuery(id+"F18.imprint","IMPRINT",FACE,{"disambiguationData":[TD([[makeQuery(id+"F18.imprint","IMPRINT",EDGE,{"derivedFrom":sQuery(id+"F18.wireOp",EDGE,"E162")}),1.0]])]});
            var Q8;
            Q8=makeQuery(id+"F19.imprint","IMPRINT",FACE,{"disambiguationData":[TD([[makeQuery(id+"F19.imprint","IMPRINT",EDGE,{"derivedFrom":sQuery(id+"F19.wireOp",EDGE,"E184")}),1.0]])]});
            var Q9;
            Q9=makeQuery(id+"F20.imprint","IMPRINT",FACE,{"disambiguationData":[TD([[makeQuery(id+"F20.imprint","IMPRINT",EDGE,{"derivedFrom":sQuery(id+"F20.wireOp",EDGE,"E206")}),1.0]])]});
            var Q10;
            Q10=makeQuery(id+"F21.imprint","IMPRINT",FACE,{"disambiguationData":[TD([[makeQuery(id+"F21.imprint","IMPRINT",EDGE,{"derivedFrom":sQuery(id+"F21.wireOp",EDGE,"E228")}),1.0]])]});
            var Q11;
            Q11=makeQuery(id+"F22.imprint","IMPRINT",FACE,{"disambiguationData":[TD([[makeQuery(id+"F22.imprint","IMPRINT",EDGE,{"derivedFrom":sQuery(id+"F22.wireOp",EDGE,"E250")}),1.0]])]});
            loft(context, id + "F24", {"sheetProfilesArray" : [{ "sheetProfileEntities" : qUnion([Q0]) }, { "sheetProfileEntities" : qUnion([Q1]) }, { "sheetProfileEntities" : qUnion([Q2]) }, { "sheetProfileEntities" : qUnion([Q3]) }, { "sheetProfileEntities" : qUnion([Q4]) }, { "sheetProfileEntities" : qUnion([Q5]) }, { "sheetProfileEntities" : qUnion([Q6]) }, { "sheetProfileEntities" : qUnion([Q7]) }, { "sheetProfileEntities" : qUnion([Q8]) }, { "sheetProfileEntities" : qUnion([Q9]) }, { "sheetProfileEntities" : qUnion([Q10]) }, { "sheetProfileEntities" : qUnion([Q11]) }]});
        }
        {
            var Q0;
            Q0=sQuery(id+"F4.wireOp",VERTEX,"E25.center");
            var Q1;
            Q1=sQuery(id+"F4.wireOp",EDGE,"E22");
            cPlane(context, id + "F25", {"entities" : qUnion([Q0, Q1]), "cplaneType" : CPlaneType.LINE_POINT, "offset" : 25.4 * mm, "width" : 152.4 * mm, "height" : 152.4 * mm});
        }
        {
            var Q0;
            Q0=qCreatedBy(id+"F25.planeOp",FACE);
            var sketch = newSketch(context, id + "F26", { "sketchPlane" : qUnion([Q0])});
            skCircle(sketch, "E252", {"center": v(-1.01, 127) * mm, "radius": 6.35 * mm});
            skSolve(sketch);
        }
        {
            var Q0;
            Q0=makeQuery(id+"F26.imprint","IMPRINT",FACE,{"disambiguationData":[TD([[makeQuery(id+"F26.imprint","IMPRINT",EDGE,{"derivedFrom":sQuery(id+"F26.wireOp",EDGE,"E252")}),1.0]])]});
            var Q1;
            Q1=sQuery(id+"F4.wireOp",EDGE,"E22");
            sweep(context, id + "F27", {"operationType" : NewBodyOperationType.ADD, "profiles" : qUnion([Q0]), "path" : qUnion([Q1])});
        }
        {
            var Q0;
            Q0=sQuery(id+"F5.wireOp",VERTEX,"E47.start");
            var Q1;
            Q1=sQuery(id+"F5.wireOp",EDGE,"E47");
            cPlane(context, id + "F28", {"entities" : qUnion([Q0, Q1]), "cplaneType" : CPlaneType.LINE_POINT, "offset" : 25.4 * mm, "width" : 152.4 * mm, "height" : 152.4 * mm});
        }
        {
            var Q0;
            Q0=qCreatedBy(id+"F28.planeOp",FACE);
            var sketch = newSketch(context, id + "F29", { "sketchPlane" : qUnion([Q0])});
            skCircle(sketch, "E253", {"center": v(1.01, 254) * mm, "radius": 6.35 * mm});
            skSolve(sketch);
        }
        {
            var Q0;
            Q0 = qSketchRegion(id + "F29", true);
            var Q1;
            Q1=sQuery(id+"F29.wireOp",EDGE,"E253");
            var Q2;
            Q2=sQuery(id+"F5.wireOp",EDGE,"E47");
            sweep(context, id + "F30", {"operationType" : NewBodyOperationType.ADD, "profiles" : qUnion([Q0]), "surfaceProfiles" : qUnion([Q1]), "path" : qUnion([Q2])});
        }
        {
            var Q0;
            Q0=sQuery(id+"F6.wireOp",VERTEX,"E69.end");
            var Q1;
            Q1=sQuery(id+"F6.wireOp",EDGE,"E69");
            cPlane(context, id + "F31", {"entities" : qUnion([Q0, Q1]), "cplaneType" : CPlaneType.LINE_POINT, "offset" : 25.4 * mm, "width" : 152.4 * mm, "height" : 152.4 * mm});
        }
        {
            var Q0;
            Q0=qCreatedBy(id+"F31.planeOp",FACE);
            var sketch = newSketch(context, id + "F32", { "sketchPlane" : qUnion([Q0])});
            skCircle(sketch, "E254", {"center": v(-2.76, 381) * mm, "radius": 6.35 * mm});
            skSolve(sketch);
        }
        {
            var Q0;
            Q0 = qSketchRegion(id + "F32", true);
            var Q1;
            Q1=sQuery(id+"F6.wireOp",EDGE,"E69");
            sweep(context, id + "F33", {"operationType" : NewBodyOperationType.ADD, "profiles" : qUnion([Q0]), "path" : qUnion([Q1])});
        }
        {
            var Q0;
            Q0=sQuery(id+"F15.wireOp",VERTEX,"E96.center");
            var Q1;
            Q1=sQuery(id+"F15.wireOp",EDGE,"E91.MirrorCS");
            cPlane(context, id + "F34", {"entities" : qUnion([Q0, Q1]), "cplaneType" : CPlaneType.LINE_POINT, "offset" : 25.4 * mm, "width" : 152.4 * mm, "height" : 152.4 * mm});
        }
        {
            var Q0;
            Q0=qCreatedBy(id+"F34.planeOp",FACE);
            var sketch = newSketch(context, id + "F35", { "sketchPlane" : qUnion([Q0])});
            skCircle(sketch, "E255", {"center": v(3.77, 508) * mm, "radius": 6.35 * mm});
            skSolve(sketch);
        }
        {
            var Q0;
            Q0 = qSketchRegion(id + "F35", true);
            var Q1;
            Q1=sQuery(id+"F15.wireOp",EDGE,"E91.MirrorCS");
            sweep(context, id + "F36", {"operationType" : NewBodyOperationType.ADD, "profiles" : qUnion([Q0]), "path" : qUnion([Q1])});
        }
        {
            var Q0;
            Q0=sQuery(id+"F16.wireOp",VERTEX,"E118.center");
            var Q1;
            Q1=sQuery(id+"F16.wireOp",EDGE,"E113.MirrorCS");
            cPlane(context, id + "F37", {"entities" : qUnion([Q0, Q1]), "cplaneType" : CPlaneType.LINE_POINT, "offset" : 25.4 * mm, "width" : 152.4 * mm, "height" : 152.4 * mm});
        }
        {
            var Q0;
            Q0=qCreatedBy(id+"F37.planeOp",FACE);
            var sketch = newSketch(context, id + "F38", { "sketchPlane" : qUnion([Q0])});
            skCircle(sketch, "E256", {"center": v(3.77, 635) * mm, "radius": 6.35 * mm});
            skSolve(sketch);
        }
        {
            var Q0;
            Q0 = qSketchRegion(id + "F38", true);
            var Q1;
            Q1=sQuery(id+"F16.wireOp",EDGE,"E113.MirrorCS");
            sweep(context, id + "F39", {"operationType" : NewBodyOperationType.ADD, "profiles" : qUnion([Q0]), "path" : qUnion([Q1])});
        }
        {
            var Q0;
            Q0=sQuery(id+"F17.wireOp",VERTEX,"E140.center");
            var Q1;
            Q1=sQuery(id+"F17.wireOp",EDGE,"E135");
            cPlane(context, id + "F40", {"entities" : qUnion([Q0, Q1]), "cplaneType" : CPlaneType.LINE_POINT, "offset" : 25.4 * mm, "width" : 152.4 * mm, "height" : 152.4 * mm});
        }
        {
            var Q0;
            Q0=qCreatedBy(id+"F40.planeOp",FACE);
            var sketch = newSketch(context, id + "F41", { "sketchPlane" : qUnion([Q0])});
            skCircle(sketch, "E257", {"center": v(-2.76, 762) * mm, "radius": 6.35 * mm});
            skSolve(sketch);
        }
        {
            var Q0;
            Q0 = qSketchRegion(id + "F41", true);
            var Q1;
            Q1=sQuery(id+"F17.wireOp",EDGE,"E135");
            sweep(context, id + "F42", {"operationType" : NewBodyOperationType.ADD, "profiles" : qUnion([Q0]), "path" : qUnion([Q1])});
        }
        {
            var Q0;
            Q0=sQuery(id+"F18.wireOp",VERTEX,"E162.center");
            var Q1;
            Q1=sQuery(id+"F18.wireOp",EDGE,"E148");
            cPlane(context, id + "F43", {"entities" : qUnion([Q0, Q1]), "cplaneType" : CPlaneType.LINE_POINT, "offset" : 25.4 * mm, "width" : 152.4 * mm, "height" : 152.4 * mm});
        }
        {
            var Q0;
            Q0=qCreatedBy(id+"F43.planeOp",FACE);
            var sketch = newSketch(context, id + "F44", { "sketchPlane" : qUnion([Q0])});
            skCircle(sketch, "E258", {"center": v(-1.01, 889) * mm, "radius": 6.35 * mm});
            skSolve(sketch);
        }
        {
            var Q0;
            Q0 = qSketchRegion(id + "F44", true);
            var Q1;
            Q1=sQuery(id+"F18.wireOp",EDGE,"E148");
            sweep(context, id + "F45", {"operationType" : NewBodyOperationType.ADD, "profiles" : qUnion([Q0]), "path" : qUnion([Q1])});
        }
        {
            var Q0;
            Q0=sQuery(id+"F19.wireOp",VERTEX,"E184.center");
            var Q1;
            Q1=sQuery(id+"F19.wireOp",EDGE,"E173");
            cPlane(context, id + "F46", {"entities" : qUnion([Q0, Q1]), "cplaneType" : CPlaneType.LINE_POINT, "offset" : 25.4 * mm, "width" : 152.4 * mm, "height" : 152.4 * mm});
        }
        {
            var Q0;
            Q0=qCreatedBy(id+"F46.planeOp",FACE);
            var sketch = newSketch(context, id + "F47", { "sketchPlane" : qUnion([Q0])});
            skCircle(sketch, "E259", {"center": v(1.01, 1016) * mm, "radius": 6.35 * mm});
            skSolve(sketch);
        }
        {
            var Q0;
            Q0 = qSketchRegion(id + "F47", true);
            var Q1;
            Q1=sQuery(id+"F19.wireOp",EDGE,"E173");
            sweep(context, id + "F48", {"operationType" : NewBodyOperationType.ADD, "profiles" : qUnion([Q0]), "path" : qUnion([Q1])});
        }
        {
            var Q0;
            Q0=sQuery(id+"F20.wireOp",VERTEX,"E206.center");
            var Q1;
            Q1=sQuery(id+"F20.wireOp",EDGE,"E195");
            cPlane(context, id + "F49", {"entities" : qUnion([Q0, Q1]), "cplaneType" : CPlaneType.LINE_POINT, "offset" : 25.4 * mm, "width" : 152.4 * mm, "height" : 152.4 * mm});
        }
        {
            var Q0;
            Q0=qCreatedBy(id+"F49.planeOp",FACE);
            var sketch = newSketch(context, id + "F50", { "sketchPlane" : qUnion([Q0])});
            skCircle(sketch, "E260", {"center": v(-2.76, 1143) * mm, "radius": 6.35 * mm});
            skSolve(sketch);
        }
        {
            var Q0;
            Q0 = qSketchRegion(id + "F50", true);
            var Q1;
            Q1=sQuery(id+"F20.wireOp",EDGE,"E195");
            sweep(context, id + "F51", {"operationType" : NewBodyOperationType.ADD, "profiles" : qUnion([Q0]), "path" : qUnion([Q1])});
        }
        {
            var Q0;
            Q0=sQuery(id+"F21.wireOp",VERTEX,"E228.center");
            var Q1;
            Q1=sQuery(id+"F21.wireOp",EDGE,"E217.MirrorCS");
            cPlane(context, id + "F52", {"entities" : qUnion([Q0, Q1]), "cplaneType" : CPlaneType.LINE_POINT, "offset" : 25.4 * mm, "width" : 152.4 * mm, "height" : 152.4 * mm});
        }
        {
            var Q0;
            Q0=qCreatedBy(id+"F52.planeOp",FACE);
            var sketch = newSketch(context, id + "F53", { "sketchPlane" : qUnion([Q0])});
            skCircle(sketch, "E261", {"center": v(3.77, 1270) * mm, "radius": 6.35 * mm});
            skSolve(sketch);
        }
        {
            var Q0;
            Q0 = qSketchRegion(id + "F53", true);
            var Q1;
            Q1=sQuery(id+"F21.wireOp",EDGE,"E217.MirrorCS");
            sweep(context, id + "F54", {"operationType" : NewBodyOperationType.ADD, "profiles" : qUnion([Q0]), "path" : qUnion([Q1])});
        }
        {
            var Q0;
            Q0=qCreatedBy(makeId("Top.planeOp"),FACE);
            var sketch = newSketch(context, id + "F55", { "sketchPlane" : qUnion([Q0])});
            skCircle(sketch, "E262", {"center": v(-0.91, 0) * mm, "radius": 3.18 * mm});
            skSolve(sketch);
        }
        {
            var Q0;
            Q0 = qSketchRegion(id + "F55", true);
            extrude(context, id + "F56", {"entities" : qUnion([Q0]), "operationType" : NewBodyOperationType.ADD, "depth" : 1270 * mm, "offsetDistance" : 25.4 * mm});
        }
    });
